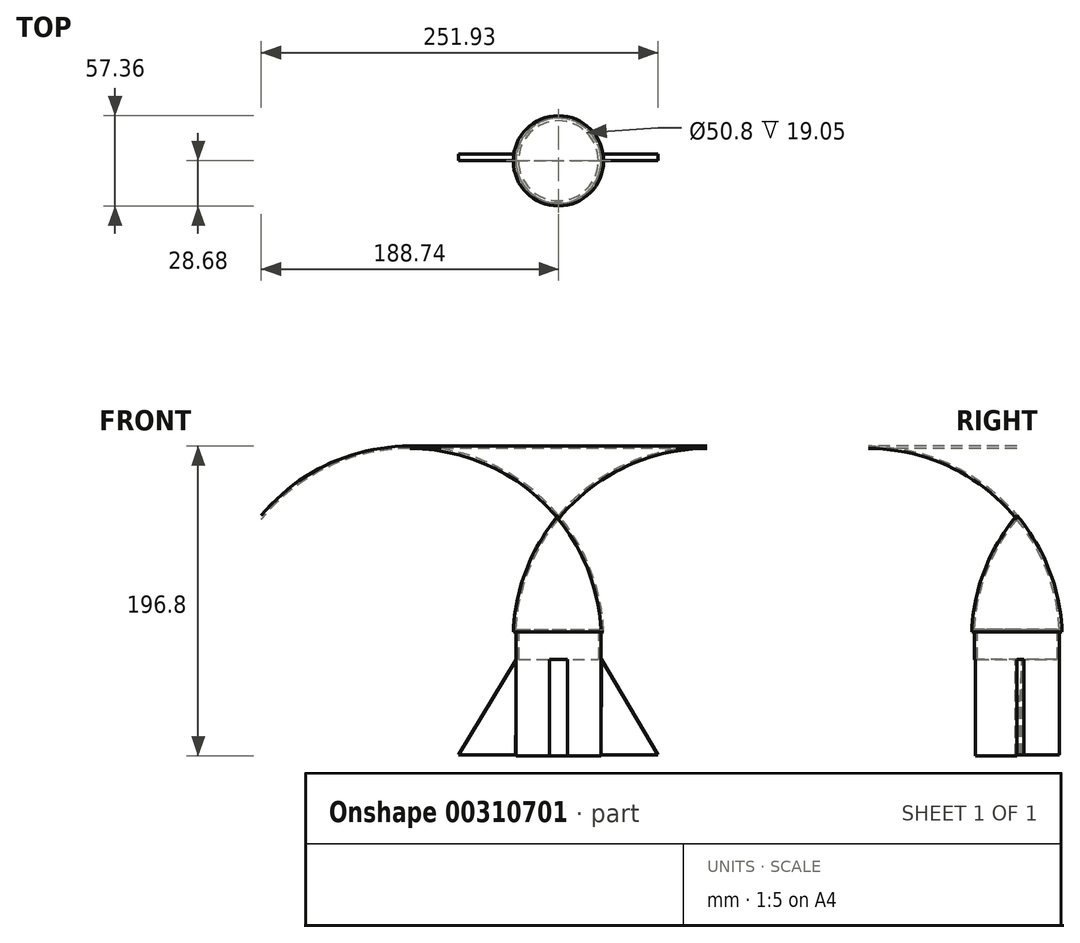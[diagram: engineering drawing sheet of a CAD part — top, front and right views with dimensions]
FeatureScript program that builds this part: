
annotation { "Feature Type Name" : "Feature", "Feature Type Description" : "" }
export const myFeature = defineFeature(function(context is Context, id is Id, definition is map)
    precondition{}
    {
        {
            var Q0;
            Q0=qCreatedBy(makeId("Front.planeOp"),FACE);
            var sketch = newSketch(context, id + "F0", { "sketchPlane" : qUnion([Q0])});
            skLineSegment(sketch, "E0", {"start": v(0, 0) * mm, "end": v(0, 88.9) * mm});
            skLineSegment(sketch, "E1", {"start": v(25.4, 0) * mm, "end": v(25.4, 19.05) * mm});
            skLineSegment(sketch, "E2", {"start": v(25.4, 19.05) * mm, "end": v(27, 19.05) * mm});
            skArc(sketch, "E3", {"start": v(27, 19.05) * mm, "mid": v(19.01, 56.1) * mm, "end": v(0, 88.9) * mm});
            skArc(sketch, "E4.0", {"start": v(28.68, 17.45) * mm, "mid": v(20.46, 56.8) * mm, "end": v(0, 91.41) * mm});
            skLineSegment(sketch, "E4.1", {"start": v(27, 17.45) * mm, "end": v(28.68, 17.45) * mm});
            skLineSegment(sketch, "E4.2", {"start": v(27, 0) * mm, "end": v(27, 17.45) * mm});
            skLineSegment(sketch, "E5", {"start": v(27, 0) * mm, "end": v(25.4, 0) * mm});
            skLineSegment(sketch, "E6", {"start": v(0, 88.9) * mm, "end": v(0, 91.41) * mm});
            skSolve(sketch);
        }
        {
            var Q0;
            Q0=makeQuery(id+"F0.imprint","IMPRINT",FACE,{"disambiguationData":[TD([[makeQuery(id+"F0.imprint","IMPRINT",EDGE,{"derivedFrom":sQuery(id+"F0.wireOp",EDGE,"E1")}),-1.0]])]});
            var Q1;
            Q1=sQuery(id+"F0.wireOp",EDGE,"E0");
            revolve(context, id + "F1", {"entities" : qUnion([Q0]), "axis" : qUnion([Q1]), "revolveType" : RevolveType.FULL});
        }
        {
            var Q0;
            Q0=qCreatedBy(makeId("Front.planeOp"),FACE);
            var sketch = newSketch(context, id + "F2", { "sketchPlane" : qUnion([Q0])});
            skLineSegment(sketch, "E7", {"start": v(-26.99, 0) * mm, "end": v(-26.99, -61.36) * mm});
            skLineSegment(sketch, "E8", {"start": v(-26.99, -61.36) * mm, "end": v(27, -61.36) * mm});
            skLineSegment(sketch, "E9", {"start": v(27, -61.36) * mm, "end": v(27, 0) * mm});
            skLineSegment(sketch, "E10", {"start": v(27, 0) * mm, "end": v(-26.99, 0) * mm});
            skSolve(sketch);
        }
        {
            var Q0;
            Q0 = qSketchRegion(id + "F2", true);
            extrude(context, id + "F3", {"entities" : qUnion([Q0]), "operationType" : NewBodyOperationType.ADD, "depth" : 26.42 * mm});
        }
        {
            var Q0;
            {var subQ0=sQuery(id+"F2.wireOp",EDGE,"E10");var subQ1=sQuery(id+"F2.wireOp",EDGE,"E7");Q0=makeQuery(id+"F3.boolean.opBoolean","SPLIT",FACE,{"disambiguationData":[TD([makeQuery(id+"F3.opExtrude","SWEPT_FACE",FACE,{"disambiguationData":[OSD([subQ1])]})])],"derivedFrom":makeQuery(id+"F3.opExtrude","SWEPT_FACE",FACE,{"disambiguationData":[OSD([subQ0])]})});}
            var Q1;
            {var subQ0=sQuery(id+"F2.wireOp",EDGE,"E10");var subQ1=sQuery(id+"F2.wireOp",EDGE,"E9");Q1=makeQuery(id+"F3.boolean.opBoolean","SPLIT",FACE,{"disambiguationData":[TD([makeQuery(id+"F3.opExtrude","SWEPT_FACE",FACE,{"disambiguationData":[OSD([subQ1])]})])],"derivedFrom":makeQuery(id+"F3.opExtrude","SWEPT_FACE",FACE,{"disambiguationData":[OSD([subQ0])]})});}
            extrude(context, id + "F4", {"entities" : qUnion([Q0, Q1]), "operationType" : NewBodyOperationType.REMOVE, "oppositeDirection" : true, "depth" : 63 * mm});
        }
        {
            var Q0;
            Q0=qCreatedBy(makeId("Front.planeOp"),FACE);
            var sketch = newSketch(context, id + "F5", { "sketchPlane" : qUnion([Q0])});
            skLineSegment(sketch, "E11", {"start": v(-26.94, 0) * mm, "end": v(-26.94, -60.87) * mm});
            skLineSegment(sketch, "E12", {"start": v(-26.94, -60.87) * mm, "end": v(26.8, -60.87) * mm});
            skLineSegment(sketch, "E13", {"start": v(26.8, -60.87) * mm, "end": v(26.8, 0) * mm});
            skLineSegment(sketch, "E14", {"start": v(26.8, 0) * mm, "end": v(-26.94, 0) * mm});
            skSolve(sketch);
        }
        {
            var Q0;
            Q0 = qSketchRegion(id + "F5", true);
            extrude(context, id + "F6", {"entities" : qUnion([Q0]), "operationType" : NewBodyOperationType.ADD, "oppositeDirection" : true, "depth" : 27.43 * mm});
        }
        {
            var Q0;
            Q0=makeQuery(id+"F6.boolean.opBoolean","SPLIT",FACE,{"derivedFrom":makeQuery(id+"F6.opExtrude","SWEPT_FACE",FACE,{"disambiguationData":[OSD([sQuery(id+"F5.wireOp",EDGE,"E14")])]})});
            extrude(context, id + "F7", {"entities" : qUnion([Q0]), "operationType" : NewBodyOperationType.REMOVE, "oppositeDirection" : true, "depth" : 68.07 * mm});
        }
        {
            var Q0;
            Q0=qCreatedBy(makeId("Front.planeOp"),FACE);
            var sketch = newSketch(context, id + "F8", { "sketchPlane" : qUnion([Q0])});
            skLineSegment(sketch, "E15", {"start": v(-26.8, 0) * mm, "end": v(-63.52, -60.87) * mm});
            skLineSegment(sketch, "E16", {"start": v(-63.52, -60.87) * mm, "end": v(-27.13, -60.87) * mm});
            skLineSegment(sketch, "E17", {"start": v(-27.13, -60.87) * mm, "end": v(-26.8, 0) * mm});
            skLineSegment(sketch, "E18", {"start": v(27.46, 0) * mm, "end": v(63.19, -60.87) * mm});
            skLineSegment(sketch, "E19", {"start": v(63.19, -60.87) * mm, "end": v(27.13, -60.87) * mm});
            skLineSegment(sketch, "E20", {"start": v(27.13, -60.87) * mm, "end": v(27.46, 0) * mm});
            skSolve(sketch);
        }
        {
            var Q0;
            Q0 = qSketchRegion(id + "F8", true);
            extrude(context, id + "F9", {"entities" : qUnion([Q0]), "operationType" : NewBodyOperationType.ADD, "oppositeDirection" : true, "depth" : 4.32 * mm});
        }
    });
